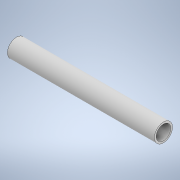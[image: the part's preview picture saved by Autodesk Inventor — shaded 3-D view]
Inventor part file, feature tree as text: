
AUTODESK INVENTOR PART (.ipt)
format: ipt  version: 2021 (Build 250183000, 183)  size: 95,232 bytes
history: native  units: mm
features: extrude x1, sketch x1
ambient origin geometry x8: Origin, YZ Plane, XZ Plane, XY Plane, X Axis, Y Axis, Z Axis, Center Point
bodies: Solid1 (feature_tree)
feature tree (2):
  extrude  "Extrusion1"  Depth=300.0mm
  sketch  "Sketch1"  dims[d0=37.0mm d1=29.625mm d2=300.0mm d3=0.0mm]
